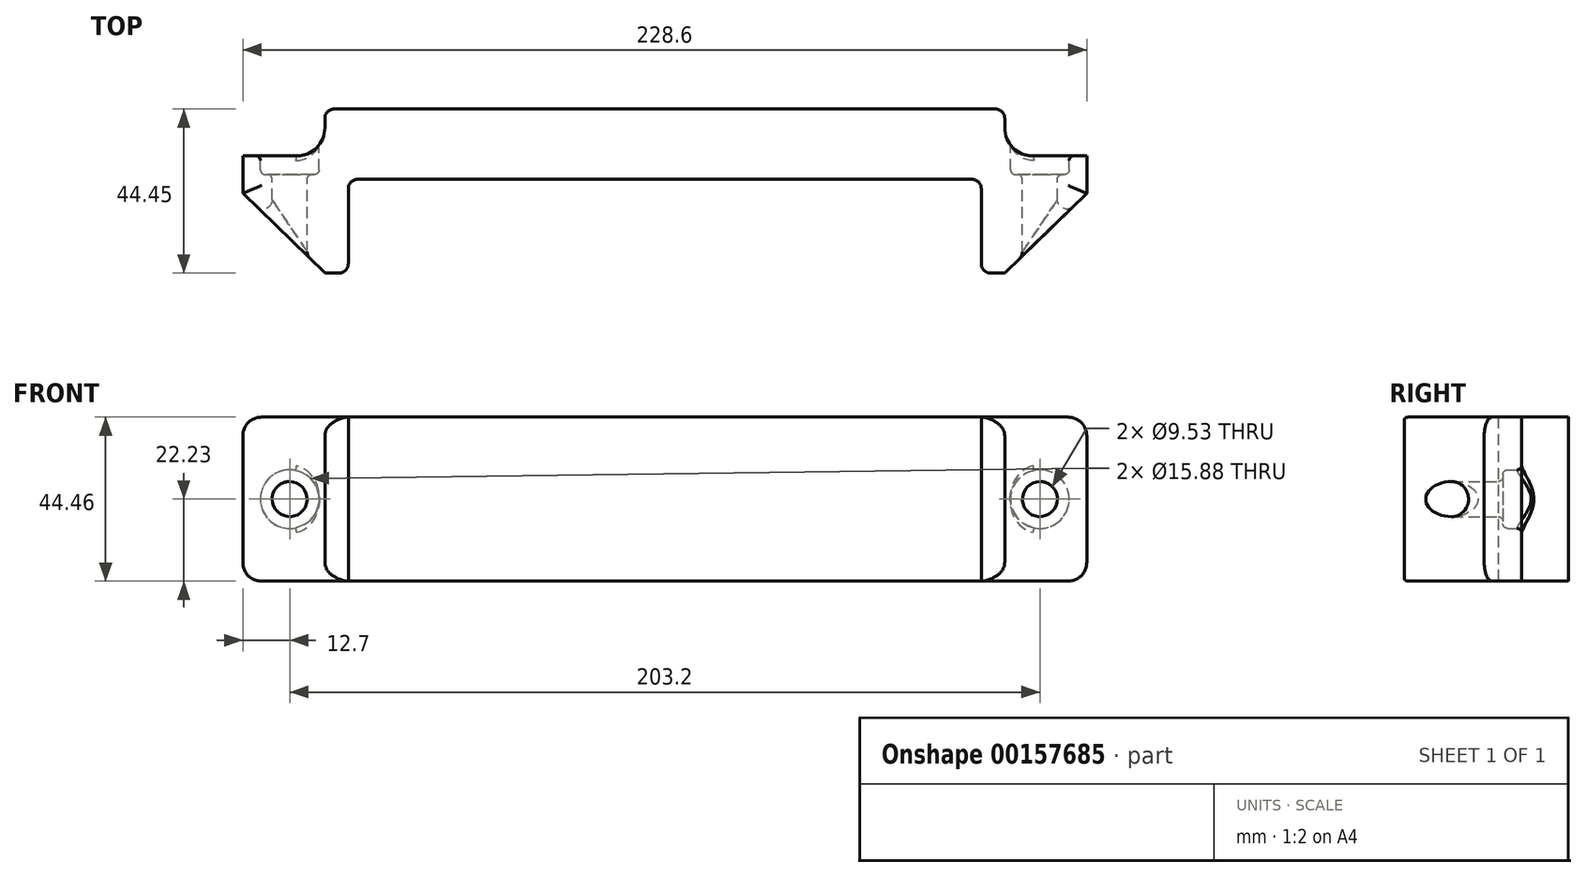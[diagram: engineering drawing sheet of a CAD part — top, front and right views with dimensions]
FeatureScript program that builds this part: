
annotation { "Feature Type Name" : "Feature", "Feature Type Description" : "" }
export const myFeature = defineFeature(function(context is Context, id is Id, definition is map)
    precondition{}
    {
        {
            var Q0;
            Q0=qCreatedBy(makeId("Top.planeOp"),FACE);
            var sketch = newSketch(context, id + "F0", { "sketchPlane" : qUnion([Q0])});
            skLineSegment(sketch, "E0", {"start": v(0, 44.45) * mm, "end": v(0, 25.4) * mm, "construction": true});
            skLineSegment(sketch, "E1", {"start": v(0, 25.4) * mm, "end": v(-83.19, 25.4) * mm});
            skLineSegment(sketch, "E2", {"start": v(-85.73, 22.86) * mm, "end": v(-85.73, 2.54) * mm});
            skLineSegment(sketch, "E3", {"start": v(-88.27, 0) * mm, "end": v(-92.08, 0) * mm});
            skLineSegment(sketch, "E4", {"start": v(-92.08, 0) * mm, "end": v(-92.08, 31.75) * mm, "construction": true});
            skLineSegment(sketch, "E5", {"start": v(-99.7, 31.75) * mm, "end": v(-92.08, 31.75) * mm});
            skLineSegment(sketch, "E6", {"start": v(-92.08, 39.37) * mm, "end": v(-92.08, 41.9) * mm});
            skLineSegment(sketch, "E7", {"start": v(-89.54, 44.45) * mm, "end": v(0, 44.45) * mm});
            skPoint(sketch, "E8.visualSharp", {"position": v(-92.08, 31.75) * mm});
            skArc(sketch, "E8.filletArc", {"start": v(-99.7, 31.75) * mm, "mid": v(-94.3, 33.98) * mm, "end": v(-92.08, 39.37) * mm});
            skPoint(sketch, "E9.visualSharp", {"position": v(-85.73, 0) * mm});
            skArc(sketch, "E9.filletArc", {"start": v(-88.27, 0) * mm, "mid": v(-86.47, 0.74) * mm, "end": v(-85.73, 2.54) * mm});
            skPoint(sketch, "E10.visualSharp", {"position": v(-92.08, 44.45) * mm});
            skArc(sketch, "E10.filletArc", {"start": v(-89.54, 44.45) * mm, "mid": v(-91.33, 43.7) * mm, "end": v(-92.08, 41.9) * mm});
            skPoint(sketch, "E11.visualSharp", {"position": v(-85.73, 25.4) * mm});
            skArc(sketch, "E11.filletArc", {"start": v(-83.19, 25.4) * mm, "mid": v(-84.98, 24.66) * mm, "end": v(-85.73, 22.86) * mm});
            skLineSegment(sketch, "E12.MirrorCS", {"start": v(85.73, 22.86) * mm, "end": v(85.73, 2.54) * mm});
            skArc(sketch, "E13.MirrorCS", {"start": v(89.54, 44.45) * mm, "mid": v(91.33, 43.7) * mm, "end": v(92.08, 41.91) * mm});
            skArc(sketch, "E14.MirrorCS", {"start": v(88.27, 0) * mm, "mid": v(86.47, 0.74) * mm, "end": v(85.73, 2.54) * mm});
            skArc(sketch, "E15.MirrorCS", {"start": v(83.19, 25.4) * mm, "mid": v(84.98, 24.66) * mm, "end": v(85.73, 22.86) * mm});
            skLineSegment(sketch, "E16.MirrorCS", {"start": v(88.27, 0) * mm, "end": v(92.08, 0) * mm});
            skArc(sketch, "E17.MirrorCS", {"start": v(99.7, 31.75) * mm, "mid": v(94.3, 33.98) * mm, "end": v(92.08, 39.37) * mm});
            skLineSegment(sketch, "E18.MirrorCS", {"start": v(92.08, 39.37) * mm, "end": v(92.08, 41.91) * mm});
            skLineSegment(sketch, "E19.MirrorCS", {"start": v(89.54, 44.45) * mm, "end": v(0, 44.45) * mm});
            skPoint(sketch, "E20.MirrorP", {"position": v(92.08, 44.45) * mm});
            skLineSegment(sketch, "E21.MirrorCS", {"start": v(0, 25.4) * mm, "end": v(83.19, 25.4) * mm});
            skPoint(sketch, "E22.MirrorP", {"position": v(85.73, 0) * mm});
            skPoint(sketch, "E23.MirrorP", {"position": v(85.73, 25.4) * mm});
            skLineSegment(sketch, "E24.MirrorCS", {"start": v(99.7, 31.75) * mm, "end": v(92.08, 31.75) * mm});
            skLineSegment(sketch, "E25.MirrorCS", {"start": v(92.08, 0) * mm, "end": v(92.08, 31.75) * mm, "construction": true});
            skPoint(sketch, "E26.MirrorP", {"position": v(92.08, 31.75) * mm});
            skLineSegment(sketch, "E27", {"start": v(-92.08, 31.75) * mm, "end": v(-114.3, 31.75) * mm});
            skLineSegment(sketch, "E28", {"start": v(-114.3, 31.75) * mm, "end": v(-114.3, 21.59) * mm});
            skLineSegment(sketch, "E29", {"start": v(-114.3, 21.59) * mm, "end": v(-92.08, 0) * mm});
            skLineSegment(sketch, "E30.MirrorCS", {"start": v(114.3, 21.6) * mm, "end": v(92.08, 0) * mm});
            skLineSegment(sketch, "E31.MirrorCS", {"start": v(92.08, 31.75) * mm, "end": v(114.3, 31.75) * mm});
            skLineSegment(sketch, "E32.MirrorCS", {"start": v(114.3, 31.75) * mm, "end": v(114.3, 21.6) * mm});
            skSolve(sketch);
        }
        {
            var Q0;
            Q0 = qSketchRegion(id + "F0", true);
            extrude(context, id + "F1", {"entities" : qUnion([Q0]), "endBound" : BoundingType.SYMMETRIC, "depth" : 44.45 * mm});
        }
        {
            var Q0;
            Q0=makeQuery(id+"F1.opExtrude","SWEPT_FACE",FACE,{"disambiguationData":[OSD([sQuery(id+"F0.wireOp",EDGE,"E7"),sQuery(id+"F0.wireOp",EDGE,"E19.MirrorCS")])]});
            var sketch = newSketch(context, id + "F2", { "sketchPlane" : qUnion([Q0])});
            skLineSegment(sketch, "E33", {"start": v(0, 0) * mm, "end": v(-101.6, 0) * mm, "construction": true});
            skCircle(sketch, "E34", {"center": v(-101.6, 0) * mm, "radius": 4.76 * mm});
            skLineSegment(sketch, "E35", {"start": v(0, 0) * mm, "end": v(0, 13.65) * mm, "construction": true});
            skLineSegment(sketch, "E36.MirrorCS", {"start": v(0, 0) * mm, "end": v(101.6, 0) * mm, "construction": true});
            skCircle(sketch, "E37.MirrorC", {"center": v(101.6, 0) * mm, "radius": 4.76 * mm});
            skSolve(sketch);
        }
        {
            var Q0;
            Q0 = qSketchRegion(id + "F2", true);
            extrude(context, id + "F3", {"entities" : qUnion([Q0]), "operationType" : NewBodyOperationType.REMOVE, "endBound" : BoundingType.THROUGH_ALL, "oppositeDirection" : true, "depth" : 25.4 * mm});
        }
        {
            var Q0;
            Q0=makeQuery(id+"F1.opExtrude","CAP_EDGE",EDGE,{"disambiguationData":[OSD([sQuery(id+"F0.wireOp",EDGE,"E32.MirrorCS")])],"isStart":true});
            var Q1;
            Q1=makeQuery(id+"F1.opExtrude","CAP_EDGE",EDGE,{"disambiguationData":[OSD([sQuery(id+"F0.wireOp",EDGE,"E32.MirrorCS")])],"isStart":false});
            var Q2;
            Q2=makeQuery(id+"F1.opExtrude","CAP_EDGE",EDGE,{"disambiguationData":[OSD([sQuery(id+"F0.wireOp",EDGE,"E30.MirrorCS")])],"isStart":false});
            var Q3;
            Q3=makeQuery(id+"F1.opExtrude","CAP_EDGE",EDGE,{"disambiguationData":[OSD([sQuery(id+"F0.wireOp",EDGE,"E30.MirrorCS")])],"isStart":true});
            var Q4;
            Q4=makeQuery(id+"F1.opExtrude","CAP_EDGE",EDGE,{"disambiguationData":[OSD([sQuery(id+"F0.wireOp",EDGE,"E29")])],"isStart":false});
            var Q5;
            Q5=makeQuery(id+"F1.opExtrude","CAP_EDGE",EDGE,{"disambiguationData":[OSD([sQuery(id+"F0.wireOp",EDGE,"E28")])],"isStart":false});
            var Q6;
            Q6=makeQuery(id+"F1.opExtrude","CAP_EDGE",EDGE,{"disambiguationData":[OSD([sQuery(id+"F0.wireOp",EDGE,"E28")])],"isStart":true});
            var Q7;
            Q7=makeQuery(id+"F1.opExtrude","CAP_EDGE",EDGE,{"disambiguationData":[OSD([sQuery(id+"F0.wireOp",EDGE,"E29")])],"isStart":true});
            fillet(context, id + "F4", {"entities" : qUnion([Q0, Q1, Q2, Q3, Q4, Q5, Q6, Q7]), "radius" : 5.08 * mm, "tangentPropagation" : true, "allowEdgeOverflow" : false});
        }
        {
            var Q0;
            Q0=makeQuery(id+"F1.opExtrude","SWEPT_FACE",FACE,{"disambiguationData":[OSD([sQuery(id+"F0.wireOp",EDGE,"E31.MirrorCS")])]});
            var sketch = newSketch(context, id + "F5", { "sketchPlane" : qUnion([Q0])});
            skCircle(sketch, "E38", {"center": v(-101.6, 0) * mm, "radius": 7.94 * mm});
            skLineSegment(sketch, "E39", {"start": v(0, 0) * mm, "end": v(0, 11.67) * mm, "construction": true});
            skCircle(sketch, "E40.MirrorC", {"center": v(101.6, 0) * mm, "radius": 7.94 * mm});
            skSolve(sketch);
        }
        {
            var Q0;
            Q0 = qSketchRegion(id + "F5", true);
            extrude(context, id + "F6", {"entities" : qUnion([Q0]), "operationType" : NewBodyOperationType.REMOVE, "oppositeDirection" : true, "depth" : 5.08 * mm, "hasSecondDirection" : true, "secondDirectionBound" : SecondDirectionBoundingType.THROUGH_ALL, "secondDirectionOppositeDirection" : false, "secondDirectionDepth" : 25.4 * mm});
        }
        {
            var Q0;
            Q0=makeQuery(id+"F3.boolean.opBoolean","INTERSECT",EDGE,{"derivedFrom":[makeQuery(id+"F1.opExtrude","SWEPT_FACE",FACE,{"disambiguationData":[OSD([sQuery(id+"F0.wireOp",EDGE,"E30.MirrorCS")])]}),makeQuery(id+"F3.opExtrude","SWEPT_FACE",FACE,{"disambiguationData":[OSD([sQuery(id+"F2.wireOp",EDGE,"E34")])]})]});
            var Q1;
            Q1=makeQuery(id+"F3.boolean.opBoolean","INTERSECT",EDGE,{"derivedFrom":[makeQuery(id+"F1.opExtrude","SWEPT_FACE",FACE,{"disambiguationData":[OSD([sQuery(id+"F0.wireOp",EDGE,"E29")])]}),makeQuery(id+"F3.opExtrude","SWEPT_FACE",FACE,{"disambiguationData":[OSD([sQuery(id+"F2.wireOp",EDGE,"E37.MirrorC")])]})]});
            fillet(context, id + "F7", {"entities" : qUnion([Q0, Q1]), "radius" : 2.54 * mm, "tangentPropagation" : true, "allowEdgeOverflow" : false});
        }
        {
            var Q0;
            Q0=makeQuery(id+"F6.boolean.opBoolean","COPY",EDGE,{"derivedFrom":makeQuery(id+"F6.opExtrude","CAP_EDGE",EDGE,{"disambiguationData":[OSD([sQuery(id+"F5.wireOp",EDGE,"E38")])],"isStart":false})});
            var Q1;
            Q1=makeQuery(id+"F6.boolean.opBoolean","COPY",EDGE,{"derivedFrom":makeQuery(id+"F6.opExtrude","CAP_EDGE",EDGE,{"disambiguationData":[OSD([sQuery(id+"F5.wireOp",EDGE,"E40.MirrorC")])],"isStart":false})});
            var Q2;
            Q2=makeQuery(id+"F3.boolean.opBoolean","COPY",FACE,{"derivedFrom":makeQuery(id+"F3.opExtrude","SWEPT_FACE",FACE,{"disambiguationData":[OSD([sQuery(id+"F2.wireOp",EDGE,"E37.MirrorC")])]})});
            var Q3;
            Q3=makeQuery(id+"F6.boolean.opBoolean","INTERSECT",EDGE,{"derivedFrom":[makeQuery(id+"F3.boolean.opBoolean","COPY",FACE,{"derivedFrom":makeQuery(id+"F3.opExtrude","SWEPT_FACE",FACE,{"disambiguationData":[OSD([sQuery(id+"F2.wireOp",EDGE,"E34")])]})}),makeQuery(id+"F6.opExtrude","CAP_FACE",FACE,{"disambiguationData":[OSD([sQuery(id+"F5.wireOp",EDGE,"E38")])],"isStart":false})]});
            var Q4;
            Q4=makeQuery(id+"F6.boolean.opBoolean","INTERSECT",EDGE,{"derivedFrom":[makeQuery(id+"F1.opExtrude","SWEPT_FACE",FACE,{"disambiguationData":[OSD([sQuery(id+"F0.wireOp",EDGE,"E31.MirrorCS")])]}),makeQuery(id+"F6.opExtrude","SWEPT_FACE",FACE,{"disambiguationData":[OSD([sQuery(id+"F5.wireOp",EDGE,"E38")])]})]});
            var Q5;
            Q5=makeQuery(id+"F6.boolean.opBoolean","INTERSECT",EDGE,{"derivedFrom":[makeQuery(id+"F1.opExtrude","SWEPT_FACE",FACE,{"disambiguationData":[OSD([sQuery(id+"F0.wireOp",EDGE,"E27")])]}),makeQuery(id+"F6.opExtrude","SWEPT_FACE",FACE,{"disambiguationData":[OSD([sQuery(id+"F5.wireOp",EDGE,"E40.MirrorC")])]})]});
            fillet(context, id + "F8", {"entities" : qUnion([Q0, Q1, Q2, Q3, Q4, Q5]), "radius" : 1.27 * mm, "tangentPropagation" : true, "allowEdgeOverflow" : false});
        }
    });
